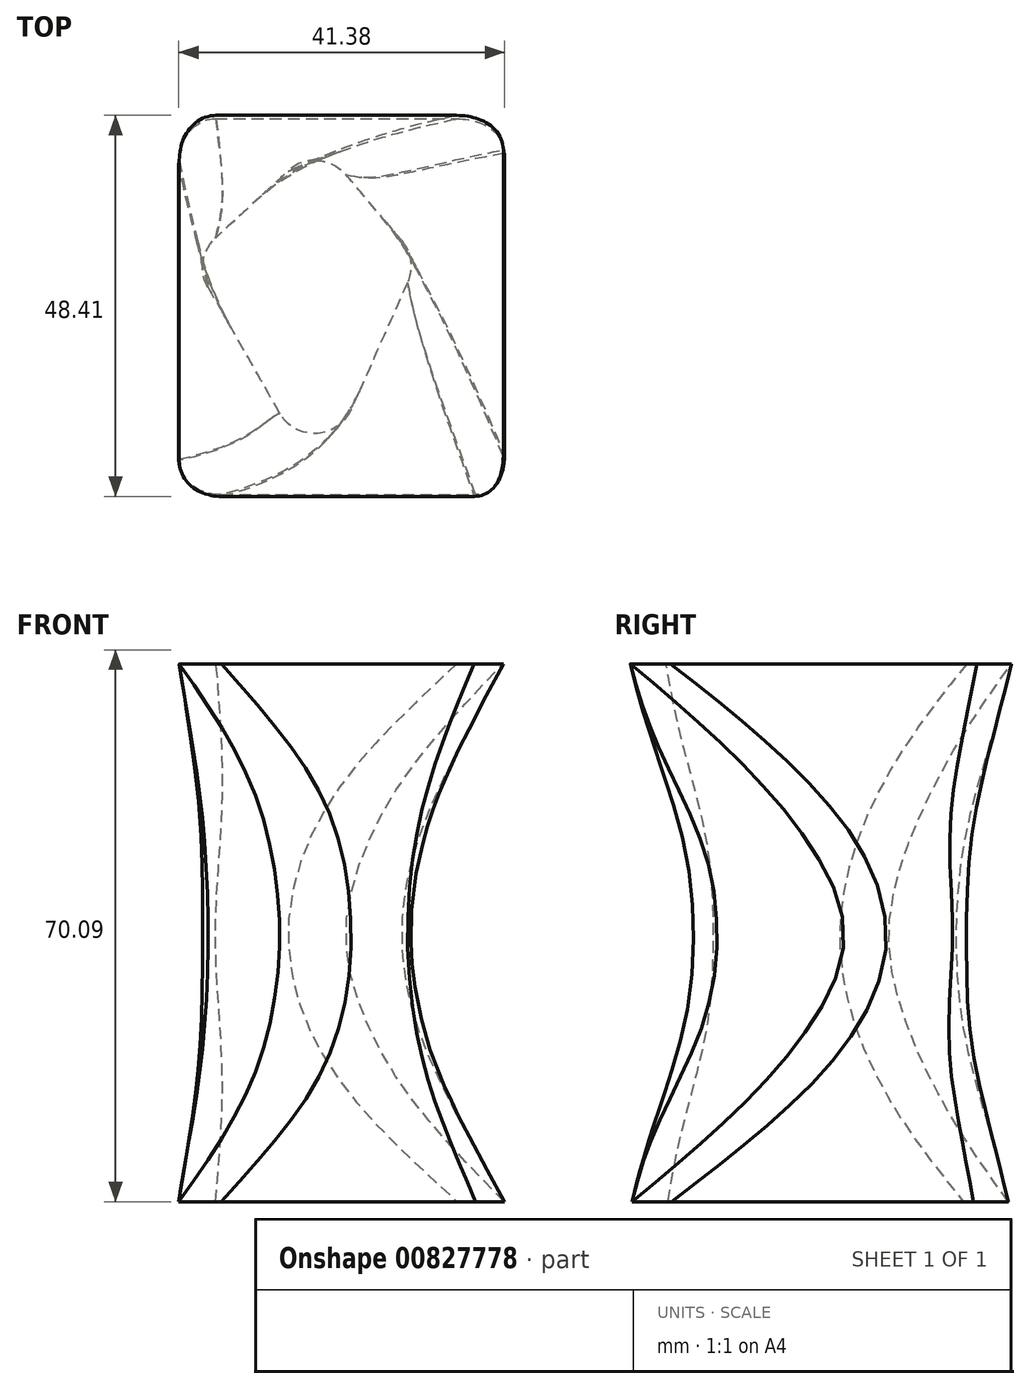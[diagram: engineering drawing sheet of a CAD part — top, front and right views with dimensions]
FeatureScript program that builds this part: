
annotation { "Feature Type Name" : "Feature", "Feature Type Description" : "" }
export const myFeature = defineFeature(function(context is Context, id is Id, definition is map)
    precondition{}
    {
        {
            var Q0;
            Q0=qCreatedBy(makeId("Top.planeOp"),FACE);
            cPlane(context, id + "F0", {"entities" : qUnion([Q0]), "cplaneType" : CPlaneType.OFFSET, "offset" : 33.27 * mm, "width" : 152.4 * mm, "height" : 152.4 * mm});
        }
        {
            var Q0;
            Q0=qCreatedBy(id+"F0.planeOp",FACE);
            cPlane(context, id + "F1", {"entities" : qUnion([Q0]), "cplaneType" : CPlaneType.OFFSET, "offset" : 35.05 * mm, "width" : 152.4 * mm, "height" : 152.4 * mm});
        }
        {
            var Q0;
            Q0=qCreatedBy(makeId("Top.planeOp"),FACE);
            var sketch = newSketch(context, id + "F2", { "sketchPlane" : qUnion([Q0])});
            skLineSegment(sketch, "E0.bottom", {"start": v(-17.81, 17.9) * mm, "end": v(23.57, 17.9) * mm});
            skLineSegment(sketch, "E0.top", {"start": v(-17.81, -29.87) * mm, "end": v(23.57, -29.87) * mm});
            skLineSegment(sketch, "E0.left", {"start": v(-17.81, 17.9) * mm, "end": v(-17.81, -29.87) * mm});
            skLineSegment(sketch, "E0.right", {"start": v(23.57, 17.9) * mm, "end": v(23.57, -29.87) * mm});
            skSolve(sketch);
        }
        {
            var Q0;
            Q0=qCreatedBy(id+"F0.planeOp",FACE);
            var sketch = newSketch(context, id + "F3", { "sketchPlane" : qUnion([Q0])});
            skLineSegment(sketch, "E1", {"start": v(0, 14.86) * mm, "end": v(-16.1, 0) * mm});
            skLineSegment(sketch, "E2", {"start": v(-16.1, 0) * mm, "end": v(0, -28.28) * mm});
            skLineSegment(sketch, "E3", {"start": v(0, -28.28) * mm, "end": v(12.55, 0) * mm});
            skLineSegment(sketch, "E4", {"start": v(12.55, 0) * mm, "end": v(0, 14.86) * mm});
            skSolve(sketch);
        }
        {
            var Q0;
            Q0=qCreatedBy(id+"F1.planeOp",FACE);
            var sketch = newSketch(context, id + "F4", { "sketchPlane" : qUnion([Q0])});
            skLineSegment(sketch, "E5.bottom", {"start": v(-17.74, 18.32) * mm, "end": v(23.42, 18.32) * mm});
            skLineSegment(sketch, "E5.top", {"start": v(-17.74, -30.09) * mm, "end": v(23.42, -30.09) * mm});
            skLineSegment(sketch, "E5.left", {"start": v(-17.74, 18.32) * mm, "end": v(-17.74, -30.09) * mm});
            skLineSegment(sketch, "E5.right", {"start": v(23.42, 18.32) * mm, "end": v(23.42, -30.09) * mm});
            skSolve(sketch);
        }
        {
            var Q0;
            Q0 = qSketchRegion(id + "F2", true);
            var Q1;
            Q1 = qSketchRegion(id + "F3", true);
            var Q2;
            Q2 = qSketchRegion(id + "F4", true);
            loft(context, id + "F5", {"sheetProfilesArray" : [{ "sheetProfileEntities" : qUnion([Q0]) }, { "sheetProfileEntities" : qUnion([Q1]) }, { "sheetProfileEntities" : qUnion([Q2]) }]});
        }
        {
            var Q0;
            Q0=makeQuery(id+"F5.opLoft","SWEPT_EDGE",EDGE,{"disambiguationData":[OSD([sQuery(id+"F2.wireOp",EDGE,"E0.bottom"),sQuery(id+"F2.wireOp",EDGE,"E0.left"),sQuery(id+"F3.wireOp",EDGE,"E1"),sQuery(id+"F3.wireOp",EDGE,"E2"),sQuery(id+"F4.wireOp",EDGE,"E5.bottom"),sQuery(id+"F4.wireOp",EDGE,"E5.left")])]});
            fillet(context, id + "F6", {"entities" : qUnion([Q0]), "radius" : 5.08 * mm, "tangentPropagation" : true, "allowEdgeOverflow" : false});
        }
        {
            var Q0;
            Q0=makeQuery(id+"F5.opLoft","SWEPT_EDGE",EDGE,{"disambiguationData":[OSD([sQuery(id+"F2.wireOp",EDGE,"E0.top"),sQuery(id+"F2.wireOp",EDGE,"E0.left"),sQuery(id+"F3.wireOp",EDGE,"E2"),sQuery(id+"F3.wireOp",EDGE,"E3"),sQuery(id+"F4.wireOp",EDGE,"E5.top"),sQuery(id+"F4.wireOp",EDGE,"E5.left")])]});
            fillet(context, id + "F7", {"entities" : qUnion([Q0]), "radius" : 5.08 * mm, "tangentPropagation" : true, "allowEdgeOverflow" : false});
        }
        {
            var Q0;
            Q0=makeQuery(id+"F5.opLoft","SWEPT_EDGE",EDGE,{"disambiguationData":[OSD([sQuery(id+"F2.wireOp",EDGE,"E0.bottom"),sQuery(id+"F2.wireOp",EDGE,"E0.right"),sQuery(id+"F3.wireOp",EDGE,"E1"),sQuery(id+"F3.wireOp",EDGE,"E4"),sQuery(id+"F4.wireOp",EDGE,"E5.bottom"),sQuery(id+"F4.wireOp",EDGE,"E5.right")])]});
            fillet(context, id + "F8", {"entities" : qUnion([Q0]), "radius" : 5.08 * mm, "tangentPropagation" : true, "allowEdgeOverflow" : false});
        }
        {
            var Q0;
            Q0=makeQuery(id+"F5.opLoft","SWEPT_EDGE",EDGE,{"disambiguationData":[OSD([sQuery(id+"F2.wireOp",EDGE,"E0.top"),sQuery(id+"F2.wireOp",EDGE,"E0.right"),sQuery(id+"F3.wireOp",EDGE,"E3"),sQuery(id+"F3.wireOp",EDGE,"E4"),sQuery(id+"F4.wireOp",EDGE,"E5.top"),sQuery(id+"F4.wireOp",EDGE,"E5.right")])]});
            fillet(context, id + "F9", {"entities" : qUnion([Q0]), "radius" : 5.08 * mm, "tangentPropagation" : true, "allowEdgeOverflow" : false});
        }
    });
